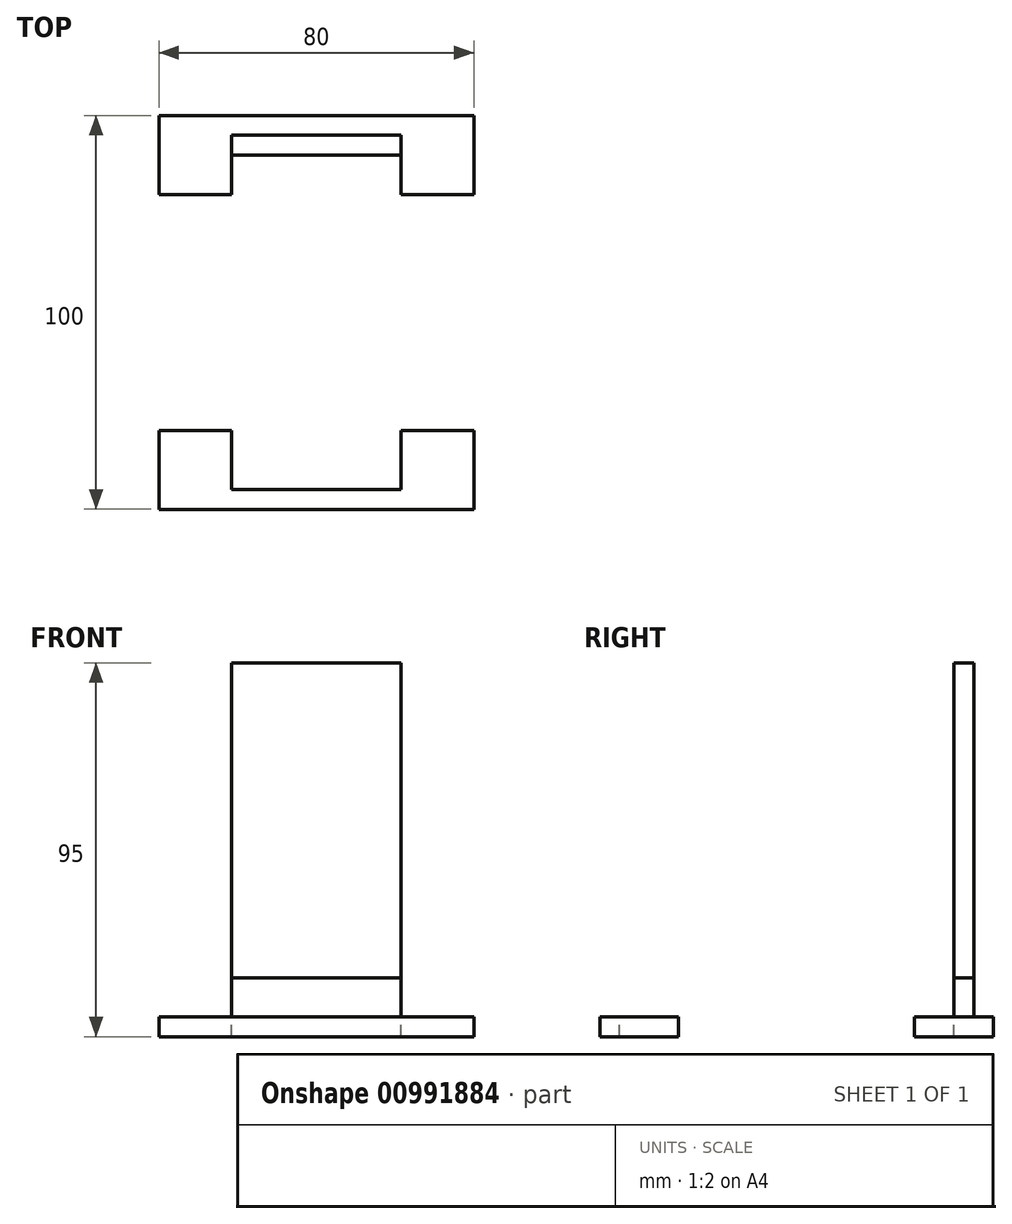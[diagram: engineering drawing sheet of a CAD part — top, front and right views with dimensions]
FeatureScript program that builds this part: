
annotation { "Feature Type Name" : "Feature", "Feature Type Description" : "" }
export const myFeature = defineFeature(function(context is Context, id is Id, definition is map)
    precondition{}
    {
        {
            var Q0;
            Q0=qCreatedBy(makeId("Top.planeOp"),FACE);
            var sketch = newSketch(context, id + "F0", { "sketchPlane" : qUnion([Q0])});
            skLineSegment(sketch, "E0.bottom", {"start": v(-40, -13.17) * mm, "end": v(40, -13.17) * mm});
            skLineSegment(sketch, "E0.top", {"start": v(-40, -33.17) * mm, "end": v(40, -33.17) * mm});
            skLineSegment(sketch, "E0.left", {"start": v(-40, -13.17) * mm, "end": v(-40, -33.17) * mm});
            skLineSegment(sketch, "E0.right", {"start": v(40, -13.17) * mm, "end": v(40, -33.17) * mm});
            skLineSegment(sketch, "E1.bottom", {"start": v(-40, 46.83) * mm, "end": v(40, 46.83) * mm});
            skLineSegment(sketch, "E1.top", {"start": v(-40, 66.83) * mm, "end": v(40, 66.83) * mm});
            skLineSegment(sketch, "E1.left", {"start": v(-40, 46.83) * mm, "end": v(-40, 66.83) * mm});
            skLineSegment(sketch, "E1.right", {"start": v(40, 46.83) * mm, "end": v(40, 66.83) * mm});
            skLineSegment(sketch, "E2", {"start": v(-40, -13.17) * mm, "end": v(40, 46.83) * mm, "construction": true});
            skLineSegment(sketch, "E3", {"start": v(-40, 46.83) * mm, "end": v(40, -13.17) * mm, "construction": true});
            skLineSegment(sketch, "E4", {"start": v(0, 16.83) * mm, "end": v(0, 90.46) * mm, "construction": true});
            skLineSegment(sketch, "E5", {"start": v(0, 16.83) * mm, "end": v(0, -55.57) * mm, "construction": true});
            skLineSegment(sketch, "E6", {"start": v(-40, -33.17) * mm, "end": v(40, -13.17) * mm, "construction": true});
            skLineSegment(sketch, "E7", {"start": v(40, 46.83) * mm, "end": v(-40, 66.83) * mm, "construction": true});
            skPoint(sketch, "E8.oppositeSnap0", {"position": v(0, 56.83) * mm});
            skLineSegment(sketch, "E8.bottom", {"start": v(-21.5, 46.83) * mm, "end": v(21.5, 46.83) * mm});
            skLineSegment(sketch, "E8.top", {"start": v(-21.5, 56.83) * mm, "end": v(21.5, 56.83) * mm});
            skLineSegment(sketch, "E8.left", {"start": v(-21.5, 46.83) * mm, "end": v(-21.5, 56.83) * mm});
            skLineSegment(sketch, "E8.right", {"start": v(21.5, 46.83) * mm, "end": v(21.5, 56.83) * mm});
            skPoint(sketch, "E9.oppositeSnap0", {"position": v(0, -23.17) * mm});
            skLineSegment(sketch, "E10", {"start": v(-60.5, 16.83) * mm, "end": v(87.32, 16.83) * mm, "construction": true});
            skLineSegment(sketch, "E11.MirrorCS", {"start": v(-21.5, -13.17) * mm, "end": v(21.5, -13.17) * mm});
            skLineSegment(sketch, "E12.MirrorCS", {"start": v(21.5, -13.17) * mm, "end": v(21.5, -23.17) * mm});
            skLineSegment(sketch, "E13.MirrorCS", {"start": v(-21.5, -13.17) * mm, "end": v(-21.5, -23.17) * mm});
            skLineSegment(sketch, "E14.MirrorCS", {"start": v(-21.5, -23.17) * mm, "end": v(21.5, -23.17) * mm});
            skLineSegment(sketch, "E15.top", {"start": v(-21.5, 61.83) * mm, "end": v(21.5, 61.83) * mm});
            skLineSegment(sketch, "E15.left", {"start": v(-21.5, 56.83) * mm, "end": v(-21.5, 61.83) * mm});
            skLineSegment(sketch, "E15.right", {"start": v(21.5, 56.83) * mm, "end": v(21.5, 61.83) * mm});
            skLineSegment(sketch, "E16.top", {"start": v(-21.5, -28.17) * mm, "end": v(21.5, -28.17) * mm});
            skLineSegment(sketch, "E16.left", {"start": v(-21.5, -23.17) * mm, "end": v(-21.5, -28.17) * mm});
            skLineSegment(sketch, "E16.right", {"start": v(21.5, -23.17) * mm, "end": v(21.5, -28.17) * mm});
            skLineSegment(sketch, "E17.bottom", {"start": v(-21.5, -13.17) * mm, "end": v(-16.5, -13.17) * mm});
            skLineSegment(sketch, "E17.top", {"start": v(-21.5, -23.17) * mm, "end": v(-16.5, -23.17) * mm});
            skLineSegment(sketch, "E17.right", {"start": v(-16.5, -13.17) * mm, "end": v(-16.5, -23.17) * mm});
            skLineSegment(sketch, "E18.bottom", {"start": v(21.5, -23.17) * mm, "end": v(16.5, -23.17) * mm});
            skLineSegment(sketch, "E18.top", {"start": v(21.5, -13.17) * mm, "end": v(16.5, -13.17) * mm});
            skLineSegment(sketch, "E18.left", {"start": v(21.5, -23.17) * mm, "end": v(21.5, -13.17) * mm});
            skLineSegment(sketch, "E18.right", {"start": v(16.5, -23.17) * mm, "end": v(16.5, -13.17) * mm});
            skLineSegment(sketch, "E19.bottom", {"start": v(-21.5, 46.83) * mm, "end": v(-16.5, 46.83) * mm});
            skLineSegment(sketch, "E19.top", {"start": v(-21.5, 56.83) * mm, "end": v(-16.5, 56.83) * mm});
            skLineSegment(sketch, "E19.right", {"start": v(-16.5, 46.83) * mm, "end": v(-16.5, 56.83) * mm});
            skLineSegment(sketch, "E20.bottom", {"start": v(21.5, 56.83) * mm, "end": v(16.5, 56.83) * mm});
            skLineSegment(sketch, "E20.top", {"start": v(21.5, 46.83) * mm, "end": v(16.5, 46.83) * mm});
            skLineSegment(sketch, "E20.left", {"start": v(21.5, 56.83) * mm, "end": v(21.5, 46.83) * mm});
            skLineSegment(sketch, "E20.right", {"start": v(16.5, 56.83) * mm, "end": v(16.5, 46.83) * mm});
            skSolve(sketch);
        }
        {
            var Q0;
            Q0=makeQuery(id+"F0.imprint","IMPRINT",FACE,{"disambiguationData":[TD([[makeQuery(id+"F0.imprint","IMPRINT",EDGE,{"derivedFrom":sQuery(id+"F0.wireOp",EDGE,"E0.top")}),1.0]])]});
            var Q1;
            Q1=makeQuery(id+"F0.imprint","IMPRINT",FACE,{"disambiguationData":[TD([[makeQuery(id+"F0.imprint","IMPRINT",EDGE,{"derivedFrom":sQuery(id+"F0.wireOp",EDGE,"E1.top")}),-1.0]])]});
            var Q2;
            Q2=makeQuery(id+"F0.imprint","IMPRINT",FACE,{"disambiguationData":[TD([[makeQuery(id+"F0.imprint","IMPRINT",EDGE,{"derivedFrom":sQuery(id+"F0.wireOp",EDGE,"E11.MirrorCS")}),-1.0]])]});
            var Q3;
            Q3=makeQuery(id+"F0.imprint","IMPRINT",FACE,{"disambiguationData":[TD([[makeQuery(id+"F0.imprint","IMPRINT",EDGE,{"derivedFrom":sQuery(id+"F0.wireOp",EDGE,"E8.bottom")}),1.0]])]});
            var Q4;
            Q4=makeQuery(id+"F0.imprint","IMPRINT",FACE,{"disambiguationData":[TD([[makeQuery(id+"F0.imprint","IMPRINT",EDGE,{"derivedFrom":sQuery(id+"F0.wireOp",EDGE,"E18.bottom")}),-1.0]])]});
            var Q5;
            Q5=makeQuery(id+"F0.imprint","IMPRINT",FACE,{"disambiguationData":[TD([[makeQuery(id+"F0.imprint","IMPRINT",EDGE,{"derivedFrom":sQuery(id+"F0.wireOp",EDGE,"E14.MirrorCS")}),-1.0]])]});
            var Q6;
            Q6=makeQuery(id+"F0.imprint","IMPRINT",FACE,{"disambiguationData":[TD([[makeQuery(id+"F0.imprint","IMPRINT",EDGE,{"derivedFrom":sQuery(id+"F0.wireOp",EDGE,"E17.bottom")}),-1.0]])]});
            var Q7;
            Q7=makeQuery(id+"F0.imprint","IMPRINT",FACE,{"disambiguationData":[TD([[makeQuery(id+"F0.imprint","IMPRINT",EDGE,{"derivedFrom":sQuery(id+"F0.wireOp",EDGE,"E20.bottom")}),1.0]])]});
            var Q8;
            Q8=makeQuery(id+"F0.imprint","IMPRINT",FACE,{"disambiguationData":[TD([[makeQuery(id+"F0.imprint","IMPRINT",EDGE,{"derivedFrom":sQuery(id+"F0.wireOp",EDGE,"E8.top")}),1.0]])]});
            var Q9;
            Q9=makeQuery(id+"F0.imprint","IMPRINT",FACE,{"disambiguationData":[TD([[makeQuery(id+"F0.imprint","IMPRINT",EDGE,{"derivedFrom":sQuery(id+"F0.wireOp",EDGE,"E19.bottom")}),1.0]])]});
            extrude(context, id + "F1", {"entities" : qUnion([Q0, Q1, Q2, Q3, Q4, Q5, Q6, Q7, Q8, Q9]), "oppositeDirection" : true, "depth" : 5 * mm, "offsetDistance" : 25 * mm});
        }
        {
            var Q0;
            Q0=makeQuery(id+"F0.imprint","IMPRINT",FACE,{"disambiguationData":[TD([[makeQuery(id+"F0.imprint","IMPRINT",EDGE,{"derivedFrom":sQuery(id+"F0.wireOp",EDGE,"E17.bottom")}),-1.0]])]});
            var Q1;
            Q1=makeQuery(id+"F0.imprint","IMPRINT",FACE,{"disambiguationData":[TD([[makeQuery(id+"F0.imprint","IMPRINT",EDGE,{"derivedFrom":sQuery(id+"F0.wireOp",EDGE,"E14.MirrorCS")}),-1.0]])]});
            var Q2;
            Q2=makeQuery(id+"F0.imprint","IMPRINT",FACE,{"disambiguationData":[TD([[makeQuery(id+"F0.imprint","IMPRINT",EDGE,{"derivedFrom":sQuery(id+"F0.wireOp",EDGE,"E18.bottom")}),-1.0]])]});
            var Q3;
            Q3=makeQuery(id+"F0.imprint","IMPRINT",FACE,{"disambiguationData":[TD([[makeQuery(id+"F0.imprint","IMPRINT",EDGE,{"derivedFrom":sQuery(id+"F0.wireOp",EDGE,"E19.bottom")}),1.0]])]});
            var Q4;
            Q4=makeQuery(id+"F0.imprint","IMPRINT",FACE,{"disambiguationData":[TD([[makeQuery(id+"F0.imprint","IMPRINT",EDGE,{"derivedFrom":sQuery(id+"F0.wireOp",EDGE,"E8.top")}),1.0]])]});
            var Q5;
            Q5=makeQuery(id+"F0.imprint","IMPRINT",FACE,{"disambiguationData":[TD([[makeQuery(id+"F0.imprint","IMPRINT",EDGE,{"derivedFrom":sQuery(id+"F0.wireOp",EDGE,"E20.bottom")}),1.0]])]});
            var Q6;
            Q6=makeQuery(id+"F0.imprint","IMPRINT",FACE,{"disambiguationData":[TD([[makeQuery(id+"F0.imprint","IMPRINT",EDGE,{"derivedFrom":sQuery(id+"F0.wireOp",EDGE,"E11.MirrorCS")}),-1.0]])]});
            var Q7;
            Q7=makeQuery(id+"F0.imprint","IMPRINT",FACE,{"disambiguationData":[TD([[makeQuery(id+"F0.imprint","IMPRINT",EDGE,{"derivedFrom":sQuery(id+"F0.wireOp",EDGE,"E8.bottom")}),1.0]])]});
            extrude(context, id + "F2", {"entities" : qUnion([Q0, Q1, Q2, Q3, Q4, Q5, Q6, Q7]), "depth" : 10 * mm, "offsetDistance" : 25 * mm});
        }
        {
            var Q0;
            Q0=makeQuery(id+"F0.imprint","IMPRINT",FACE,{"disambiguationData":[TD([[makeQuery(id+"F0.imprint","IMPRINT",EDGE,{"derivedFrom":sQuery(id+"F0.wireOp",EDGE,"E18.bottom")}),-1.0]])]});
            var Q1;
            Q1=makeQuery(id+"F0.imprint","IMPRINT",FACE,{"disambiguationData":[TD([[makeQuery(id+"F0.imprint","IMPRINT",EDGE,{"derivedFrom":sQuery(id+"F0.wireOp",EDGE,"E14.MirrorCS")}),-1.0]])]});
            var Q2;
            Q2=makeQuery(id+"F0.imprint","IMPRINT",FACE,{"disambiguationData":[TD([[makeQuery(id+"F0.imprint","IMPRINT",EDGE,{"derivedFrom":sQuery(id+"F0.wireOp",EDGE,"E17.bottom")}),-1.0]])]});
            var Q3;
            Q3=makeQuery(id+"F0.imprint","IMPRINT",FACE,{"disambiguationData":[TD([[makeQuery(id+"F0.imprint","IMPRINT",EDGE,{"derivedFrom":sQuery(id+"F0.wireOp",EDGE,"E20.bottom")}),1.0]])]});
            var Q4;
            Q4=makeQuery(id+"F0.imprint","IMPRINT",FACE,{"disambiguationData":[TD([[makeQuery(id+"F0.imprint","IMPRINT",EDGE,{"derivedFrom":sQuery(id+"F0.wireOp",EDGE,"E8.top")}),1.0]])]});
            var Q5;
            Q5=makeQuery(id+"F0.imprint","IMPRINT",FACE,{"disambiguationData":[TD([[makeQuery(id+"F0.imprint","IMPRINT",EDGE,{"derivedFrom":sQuery(id+"F0.wireOp",EDGE,"E19.bottom")}),1.0]])]});
            extrude(context, id + "F3", {"entities" : qUnion([Q0, Q1, Q2, Q3, Q4, Q5]), "depth" : 90 * mm, "offsetDistance" : 25 * mm});
        }
    });
